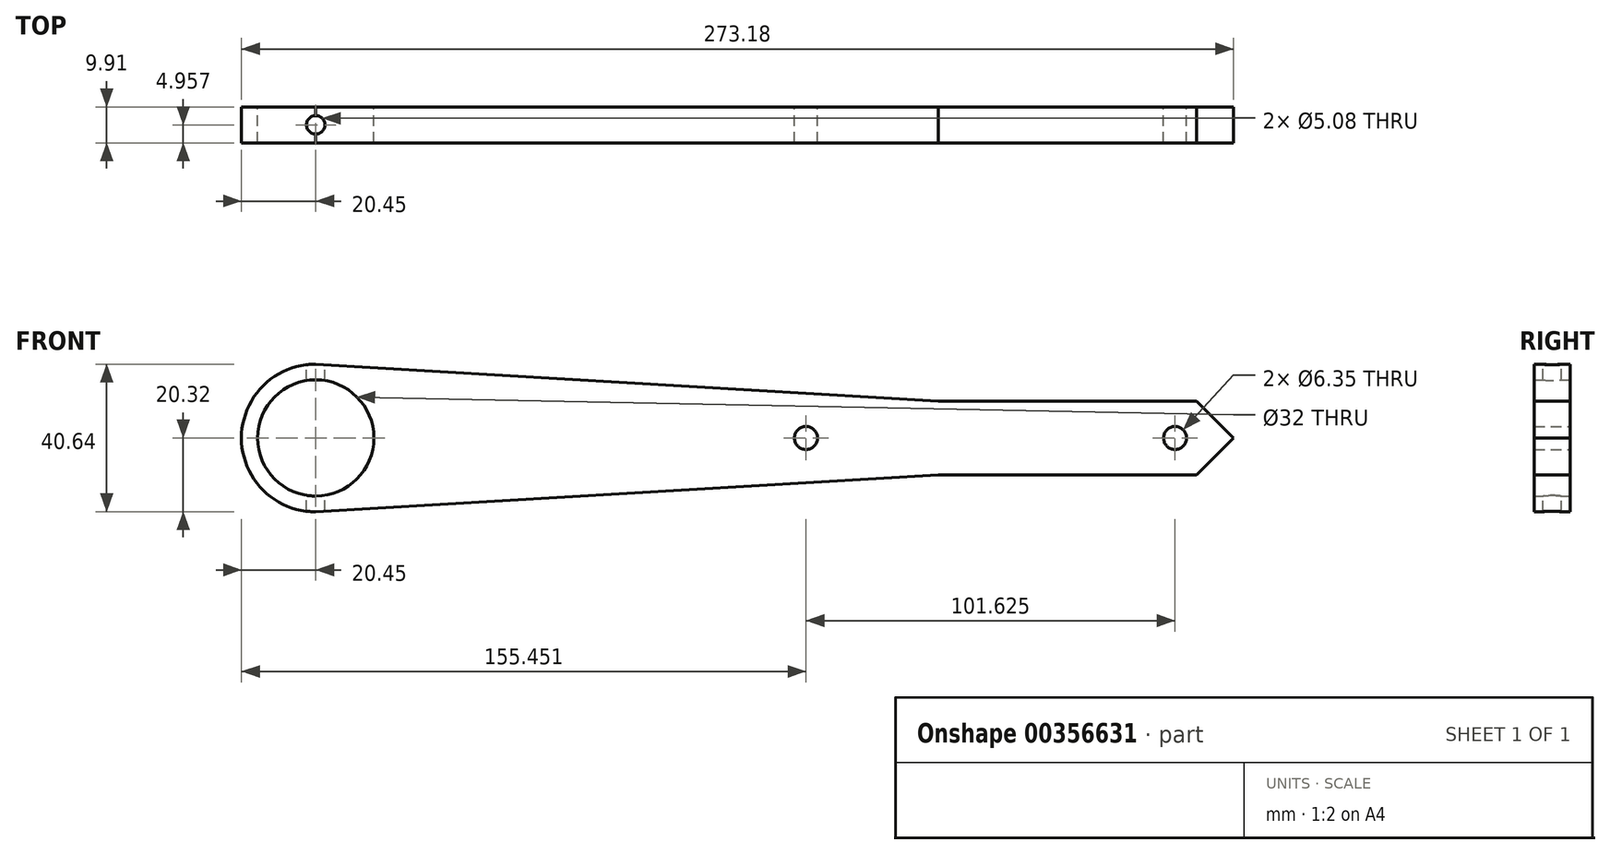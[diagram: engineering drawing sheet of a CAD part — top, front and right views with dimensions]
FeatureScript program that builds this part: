
annotation { "Feature Type Name" : "Feature", "Feature Type Description" : "" }
export const myFeature = defineFeature(function(context is Context, id is Id, definition is map)
    precondition{}
    {
        {
            var Q0;
            Q0=qCreatedBy(makeId("Front.planeOp"),FACE);
            var sketch = newSketch(context, id + "F0", { "sketchPlane" : qUnion([Q0])});
            skLineSegment(sketch, "E0.bottom", {"start": v(40.64, -10.16) * mm, "end": v(-40.64, -10.16) * mm});
            skLineSegment(sketch, "E0.top", {"start": v(40.64, 10.16) * mm, "end": v(-40.64, 10.16) * mm});
            skLineSegment(sketch, "E0.left", {"start": v(40.64, -10.16) * mm, "end": v(40.64, 10.16) * mm});
            skPoint(sketch, "E0.middle", {"position": v(0, 0) * mm});
            skLineSegment(sketch, "E1.bottom", {"start": v(-212.1, -20.32) * mm, "end": v(-212.36, -20.32) * mm});
            skLineSegment(sketch, "E1.top", {"start": v(-212.09, 20.32) * mm, "end": v(-212.36, 20.32) * mm});
            skLineSegment(sketch, "E1.right", {"start": v(-232.4, -2.34) * mm, "end": v(-232.4, 2.34) * mm});
            skPoint(sketch, "E1.middle", {"position": v(-212.1, 0) * mm});
            skCircle(sketch, "E2", {"center": v(-212.1, 0) * mm, "radius": 16 * mm});
            skArc(sketch, "E3", {"start": v(-212.09, 20.32) * mm, "mid": v(-232.54, 0) * mm, "end": v(-212.1, -20.32) * mm});
            skPoint(sketch, "E4.orphan", {"position": v(-232.4, 20.32) * mm});
            skPoint(sketch, "E5.orphan", {"position": v(-232.4, -20.32) * mm});
            skCircle(sketch, "E6", {"center": v(-77.09, 0) * mm, "radius": 3.18 * mm});
            skCircle(sketch, "E7", {"center": v(24.54, 0) * mm, "radius": 3.18 * mm});
            skLineSegment(sketch, "E8", {"start": v(-212.1, -20.32) * mm, "end": v(-40.64, -10.16) * mm});
            skLineSegment(sketch, "E9", {"start": v(-212.09, 20.32) * mm, "end": v(-40.64, 10.16) * mm});
            skLineSegment(sketch, "E10", {"start": v(-212.09, 31.09) * mm, "end": v(-212.09, -33.26) * mm, "construction": true});
            skSolve(sketch);
        }
        {
            var Q0;
            Q0 = qSketchRegion(id + "F0", true);
            extrude(context, id + "F1", {"entities" : qUnion([Q0]), "depth" : 9.9 * mm});
        }
        {
            var Q0;
            Q0=makeQuery(id+"F1.opExtrude","CAP_FACE",FACE,{"disambiguationData":[OSD([sQuery(id+"F0.wireOp",EDGE,"E0.bottom"),sQuery(id+"F0.wireOp",EDGE,"E0.top"),sQuery(id+"F0.wireOp",EDGE,"E0.left"),sQuery(id+"F0.wireOp",EDGE,"E2"),sQuery(id+"F0.wireOp",EDGE,"E3"),sQuery(id+"F0.wireOp",EDGE,"E6"),sQuery(id+"F0.wireOp",EDGE,"E7"),sQuery(id+"F0.wireOp",EDGE,"E8"),sQuery(id+"F0.wireOp",EDGE,"E9")])],"isStart":false});
            var sketch = newSketch(context, id + "F2", { "sketchPlane" : qUnion([Q0])});
            skArc(sketch, "E11.0", {"start": v(-192.22, -12.78) * mm, "mid": v(-188.48, -0.77) * mm, "end": v(-191.44, 11.46) * mm});
            skArc(sketch, "E12.0", {"start": v(-86.52, 5.25) * mm, "mid": v(-87.86, -0.73) * mm, "end": v(-85.73, -6.47) * mm});
            skLineSegment(sketch, "E13.0", {"start": v(-191.44, 11.46) * mm, "end": v(-86.52, 5.25) * mm});
            skLineSegment(sketch, "E14.0", {"start": v(-192.22, -12.78) * mm, "end": v(-85.73, -6.47) * mm});
            skSolve(sketch);
        }
        {
            var Q0;
            Q0=makeQuery(id+"F1.opExtrude","CAP_FACE",FACE,{"disambiguationData":[OSD([sQuery(id+"F0.wireOp",EDGE,"E0.bottom"),sQuery(id+"F0.wireOp",EDGE,"E0.top"),sQuery(id+"F0.wireOp",EDGE,"E0.left"),sQuery(id+"F0.wireOp",EDGE,"E2"),sQuery(id+"F0.wireOp",EDGE,"E3"),sQuery(id+"F0.wireOp",EDGE,"E6"),sQuery(id+"F0.wireOp",EDGE,"E7"),sQuery(id+"F0.wireOp",EDGE,"E8"),sQuery(id+"F0.wireOp",EDGE,"E9")])],"isStart":false});
            var sketch = newSketch(context, id + "F3", { "sketchPlane" : qUnion([Q0])});
            skLineSegment(sketch, "E15", {"start": v(-191.44, 11.46) * mm, "end": v(-138.98, -9.63) * mm});
            skLineSegment(sketch, "E16", {"start": v(-138.98, -9.63) * mm, "end": v(-86.52, 5.25) * mm});
            skLineSegment(sketch, "E17", {"start": v(-85.73, -6.47) * mm, "end": v(-138.98, 8.35) * mm});
            skLineSegment(sketch, "E18", {"start": v(-138.98, 8.35) * mm, "end": v(-192.22, -12.78) * mm});
            skLineSegment(sketch, "E19.0", {"start": v(-190.84, 12.94) * mm, "end": v(-138.39, -8.15) * mm});
            skLineSegment(sketch, "E20.0", {"start": v(-192.03, 9.99) * mm, "end": v(-139.57, -11.1) * mm});
            skLineSegment(sketch, "E21.0", {"start": v(-139.57, 9.83) * mm, "end": v(-192.81, -11.3) * mm});
            skLineSegment(sketch, "E22.0", {"start": v(-138.4, 6.88) * mm, "end": v(-191.64, -14.26) * mm});
            skLineSegment(sketch, "E23.0", {"start": v(-85.3, -4.94) * mm, "end": v(-138.55, 9.88) * mm});
            skLineSegment(sketch, "E24.0", {"start": v(-86.16, -8) * mm, "end": v(-139.4, 6.82) * mm});
            skLineSegment(sketch, "E25.0", {"start": v(-138.54, -11.15) * mm, "end": v(-86.1, 3.72) * mm});
            skLineSegment(sketch, "E26.0", {"start": v(-139.41, -8.1) * mm, "end": v(-86.96, 6.77) * mm});
            skLineSegment(sketch, "E27", {"start": v(-192.03, 9.99) * mm, "end": v(-190.84, 12.94) * mm});
            skSolve(sketch);
        }
        {
            var Q0;
            {var subQ0=sQuery(id+"F3.wireOp",EDGE,"E21.0");var subQ1=sQuery(id+"F3.wireOp",EDGE,"E15");var subQ2=makeQuery(id+"F3.imprint","INTERSECT",VERTEX,{"derivedFrom":[subQ1,subQ0]});Q0=makeQuery(id+"F3.imprint","IMPRINT",FACE,{"disambiguationData":[TD([[makeQuery(id+"F3.imprint","IMPRINT",EDGE,{"disambiguationData":[TD([[subQ2,-1.0]])],"derivedFrom":subQ1}),1.0]])]});}
            var Q1;
            {var subQ0=sQuery(id+"F3.wireOp",EDGE,"E21.0");var subQ1=sQuery(id+"F3.wireOp",EDGE,"E15");var subQ2=makeQuery(id+"F3.imprint","INTERSECT",VERTEX,{"derivedFrom":[subQ1,subQ0]});Q1=makeQuery(id+"F3.imprint","IMPRINT",FACE,{"disambiguationData":[TD([[makeQuery(id+"F3.imprint","IMPRINT",EDGE,{"disambiguationData":[TD([[subQ2,-1.0]])],"derivedFrom":subQ1}),-1.0]])]});}
            var Q2;
            {var subQ0=sQuery(id+"F3.wireOp",EDGE,"E18");var subQ1=sQuery(id+"F3.wireOp",EDGE,"E15");var subQ2=makeQuery(id+"F3.imprint","INTERSECT",VERTEX,{"derivedFrom":[subQ1,subQ0]});Q2=makeQuery(id+"F3.imprint","IMPRINT",FACE,{"disambiguationData":[TD([[makeQuery(id+"F3.imprint","IMPRINT",EDGE,{"disambiguationData":[TD([[subQ2,-1.0]])],"derivedFrom":subQ1}),1.0]])]});}
            var Q3;
            {var subQ0=sQuery(id+"F3.wireOp",EDGE,"E18");var subQ1=sQuery(id+"F3.wireOp",EDGE,"E15");var subQ2=makeQuery(id+"F3.imprint","INTERSECT",VERTEX,{"derivedFrom":[subQ1,subQ0]});Q3=makeQuery(id+"F3.imprint","IMPRINT",FACE,{"disambiguationData":[TD([[makeQuery(id+"F3.imprint","IMPRINT",EDGE,{"disambiguationData":[TD([[subQ2,-1.0]])],"derivedFrom":subQ1}),-1.0]])]});}
            var Q4;
            {var subQ0=sQuery(id+"F3.wireOp",EDGE,"E24.0");var subQ1=sQuery(id+"F3.wireOp",EDGE,"E16");var subQ2=makeQuery(id+"F3.imprint","INTERSECT",VERTEX,{"derivedFrom":[subQ1,subQ0]});Q4=makeQuery(id+"F3.imprint","IMPRINT",FACE,{"disambiguationData":[TD([[makeQuery(id+"F3.imprint","IMPRINT",EDGE,{"disambiguationData":[TD([[subQ2,-1.0]])],"derivedFrom":subQ1}),-1.0]])]});}
            var Q5;
            {var subQ0=sQuery(id+"F3.wireOp",EDGE,"E24.0");var subQ1=sQuery(id+"F3.wireOp",EDGE,"E16");var subQ2=makeQuery(id+"F3.imprint","INTERSECT",VERTEX,{"derivedFrom":[subQ1,subQ0]});Q5=makeQuery(id+"F3.imprint","IMPRINT",FACE,{"disambiguationData":[TD([[makeQuery(id+"F3.imprint","IMPRINT",EDGE,{"disambiguationData":[TD([[subQ2,-1.0]])],"derivedFrom":subQ1}),1.0]])]});}
            var Q6;
            {var subQ0=sQuery(id+"F3.wireOp",EDGE,"E17");var subQ1=sQuery(id+"F3.wireOp",EDGE,"E16");var subQ2=makeQuery(id+"F3.imprint","INTERSECT",VERTEX,{"derivedFrom":[subQ1,subQ0]});Q6=makeQuery(id+"F3.imprint","IMPRINT",FACE,{"disambiguationData":[TD([[makeQuery(id+"F3.imprint","IMPRINT",EDGE,{"disambiguationData":[TD([[subQ2,-1.0]])],"derivedFrom":subQ1}),-1.0]])]});}
            var Q7;
            {var subQ0=sQuery(id+"F3.wireOp",EDGE,"E17");var subQ1=sQuery(id+"F3.wireOp",EDGE,"E16");var subQ2=makeQuery(id+"F3.imprint","INTERSECT",VERTEX,{"derivedFrom":[subQ1,subQ0]});Q7=makeQuery(id+"F3.imprint","IMPRINT",FACE,{"disambiguationData":[TD([[makeQuery(id+"F3.imprint","IMPRINT",EDGE,{"disambiguationData":[TD([[subQ2,-1.0]])],"derivedFrom":subQ1}),1.0]])]});}
            var Q8;
            {var subQ3=sQuery(id+"F3.wireOp",EDGE,"E19.0");var subQ5=sQuery(id+"F3.wireOp",EDGE,"E26.0");var subQ6=makeQuery(id+"F3.imprint","INTERSECT",VERTEX,{"derivedFrom":[subQ3,subQ5]});Q8=makeQuery(id+"F3.imprint","IMPRINT",FACE,{"disambiguationData":[TD([[makeQuery(id+"F3.imprint","IMPRINT",EDGE,{"disambiguationData":[TD([[subQ6,1.0]])],"derivedFrom":subQ3}),-1.0]])]});}
            var Q9;
            {var subQ3=sQuery(id+"F3.wireOp",EDGE,"E19.0");var subQ5=sQuery(id+"F3.wireOp",EDGE,"E18");var subQ6=makeQuery(id+"F3.imprint","INTERSECT",VERTEX,{"derivedFrom":[subQ5,subQ3]});Q9=makeQuery(id+"F3.imprint","IMPRINT",FACE,{"disambiguationData":[TD([[makeQuery(id+"F3.imprint","IMPRINT",EDGE,{"disambiguationData":[TD([[subQ6,-1.0]])],"derivedFrom":subQ3}),1.0]])]});}
            var Q10;
            {var subQ0=sQuery(id+"F3.wireOp",EDGE,"E27");var subQ1=sQuery(id+"F3.wireOp",EDGE,"E19.0");var subQ2=makeQuery(id+"F3.imprint","INTERSECT",VERTEX,{"derivedFrom":[subQ1,subQ0]});Q10=makeQuery(id+"F3.imprint","IMPRINT",FACE,{"disambiguationData":[TD([[makeQuery(id+"F3.imprint","IMPRINT",EDGE,{"disambiguationData":[TD([[subQ2,-1.0]])],"derivedFrom":subQ1}),-1.0]])]});}
            var Q11;
            {var subQ0=sQuery(id+"F3.wireOp",EDGE,"E27");var subQ1=sQuery(id+"F3.wireOp",EDGE,"E20.0");var subQ2=makeQuery(id+"F3.imprint","INTERSECT",VERTEX,{"derivedFrom":[subQ1,subQ0]});Q11=makeQuery(id+"F3.imprint","IMPRINT",FACE,{"disambiguationData":[TD([[makeQuery(id+"F3.imprint","IMPRINT",EDGE,{"disambiguationData":[TD([[subQ2,-1.0]])],"derivedFrom":subQ1}),1.0]])]});}
            var Q12;
            {var subQ3=sQuery(id+"F3.wireOp",EDGE,"E21.0");var subQ5=sQuery(id+"F3.wireOp",EDGE,"E19.0");var subQ6=makeQuery(id+"F3.imprint","INTERSECT",VERTEX,{"derivedFrom":[subQ5,subQ3]});Q12=makeQuery(id+"F3.imprint","IMPRINT",FACE,{"disambiguationData":[TD([[makeQuery(id+"F3.imprint","IMPRINT",EDGE,{"disambiguationData":[TD([[subQ6,1.0]])],"derivedFrom":subQ5}),-1.0]])]});}
            var Q13;
            {var subQ0=sQuery(id+"F3.wireOp",EDGE,"E18");var subQ3=sQuery(id+"F3.wireOp",EDGE,"E20.0");var subQ4=makeQuery(id+"F3.imprint","INTERSECT",VERTEX,{"derivedFrom":[subQ0,subQ3]});Q13=makeQuery(id+"F3.imprint","IMPRINT",FACE,{"disambiguationData":[TD([[makeQuery(id+"F3.imprint","IMPRINT",EDGE,{"disambiguationData":[TD([[subQ4,1.0]])],"derivedFrom":subQ3}),-1.0]])]});}
            var Q14;
            {var subQ0=sQuery(id+"F3.wireOp",EDGE,"E18");var subQ3=sQuery(id+"F3.wireOp",EDGE,"E20.0");var subQ4=makeQuery(id+"F3.imprint","INTERSECT",VERTEX,{"derivedFrom":[subQ0,subQ3]});Q14=makeQuery(id+"F3.imprint","IMPRINT",FACE,{"disambiguationData":[TD([[makeQuery(id+"F3.imprint","IMPRINT",EDGE,{"disambiguationData":[TD([[subQ4,-1.0]])],"derivedFrom":subQ3}),-1.0]])]});}
            var Q15;
            {var subQ3=sQuery(id+"F3.wireOp",EDGE,"E26.0");var subQ5=sQuery(id+"F3.wireOp",EDGE,"E23.0");var subQ6=makeQuery(id+"F3.imprint","INTERSECT",VERTEX,{"derivedFrom":[subQ5,subQ3]});Q15=makeQuery(id+"F3.imprint","IMPRINT",FACE,{"disambiguationData":[TD([[makeQuery(id+"F3.imprint","IMPRINT",EDGE,{"disambiguationData":[TD([[subQ6,-1.0]])],"derivedFrom":subQ5}),1.0]])]});}
            var Q16;
            {var subQ0=sQuery(id+"F3.wireOp",EDGE,"E18");var subQ3=sQuery(id+"F3.wireOp",EDGE,"E19.0");var subQ4=makeQuery(id+"F3.imprint","INTERSECT",VERTEX,{"derivedFrom":[subQ0,subQ3]});Q16=makeQuery(id+"F3.imprint","IMPRINT",FACE,{"disambiguationData":[TD([[makeQuery(id+"F3.imprint","IMPRINT",EDGE,{"disambiguationData":[TD([[subQ4,1.0]])],"derivedFrom":subQ3}),1.0]])]});}
            var Q17;
            {var subQ0=sQuery(id+"F3.wireOp",EDGE,"E16");var subQ3=sQuery(id+"F3.wireOp",EDGE,"E23.0");var subQ4=makeQuery(id+"F3.imprint","INTERSECT",VERTEX,{"derivedFrom":[subQ0,subQ3]});Q17=makeQuery(id+"F3.imprint","IMPRINT",FACE,{"disambiguationData":[TD([[makeQuery(id+"F3.imprint","IMPRINT",EDGE,{"disambiguationData":[TD([[subQ4,1.0]])],"derivedFrom":subQ3}),-1.0]])]});}
            var Q18;
            {var subQ0=sQuery(id+"F3.wireOp",EDGE,"E16");var subQ3=sQuery(id+"F3.wireOp",EDGE,"E23.0");var subQ4=makeQuery(id+"F3.imprint","INTERSECT",VERTEX,{"derivedFrom":[subQ0,subQ3]});Q18=makeQuery(id+"F3.imprint","IMPRINT",FACE,{"disambiguationData":[TD([[makeQuery(id+"F3.imprint","IMPRINT",EDGE,{"disambiguationData":[TD([[subQ4,-1.0]])],"derivedFrom":subQ3}),-1.0]])]});}
            var Q19;
            {var subQ3=sQuery(id+"F3.wireOp",EDGE,"E25.0");var subQ5=sQuery(id+"F3.wireOp",EDGE,"E23.0");var subQ6=makeQuery(id+"F3.imprint","INTERSECT",VERTEX,{"derivedFrom":[subQ5,subQ3]});Q19=makeQuery(id+"F3.imprint","IMPRINT",FACE,{"disambiguationData":[TD([[makeQuery(id+"F3.imprint","IMPRINT",EDGE,{"disambiguationData":[TD([[subQ6,1.0]])],"derivedFrom":subQ5}),1.0]])]});}
            var Q20;
            {var subQ3=sQuery(id+"F3.wireOp",EDGE,"E25.0");var subQ5=sQuery(id+"F3.wireOp",EDGE,"E24.0");var subQ6=makeQuery(id+"F3.imprint","INTERSECT",VERTEX,{"derivedFrom":[subQ5,subQ3]});Q20=makeQuery(id+"F3.imprint","IMPRINT",FACE,{"disambiguationData":[TD([[makeQuery(id+"F3.imprint","IMPRINT",EDGE,{"disambiguationData":[TD([[subQ6,1.0]])],"derivedFrom":subQ5}),-1.0]])]});}
            var Q21;
            {var subQ0=sQuery(id+"F3.wireOp",EDGE,"E16");var subQ3=sQuery(id+"F3.wireOp",EDGE,"E24.0");var subQ4=makeQuery(id+"F3.imprint","INTERSECT",VERTEX,{"derivedFrom":[subQ0,subQ3]});Q21=makeQuery(id+"F3.imprint","IMPRINT",FACE,{"disambiguationData":[TD([[makeQuery(id+"F3.imprint","IMPRINT",EDGE,{"disambiguationData":[TD([[subQ4,1.0]])],"derivedFrom":subQ3}),1.0]])]});}
            var Q22;
            {var subQ3=sQuery(id+"F3.wireOp",EDGE,"E22.0");var subQ5=sQuery(id+"F3.wireOp",EDGE,"E20.0");var subQ6=makeQuery(id+"F3.imprint","INTERSECT",VERTEX,{"derivedFrom":[subQ5,subQ3]});Q22=makeQuery(id+"F3.imprint","IMPRINT",FACE,{"disambiguationData":[TD([[makeQuery(id+"F3.imprint","IMPRINT",EDGE,{"disambiguationData":[TD([[subQ6,-1.0]])],"derivedFrom":subQ5}),1.0]])]});}
            var Q23;
            {var subQ3=sQuery(id+"F3.wireOp",EDGE,"E21.0");var subQ5=sQuery(id+"F3.wireOp",EDGE,"E20.0");var subQ6=makeQuery(id+"F3.imprint","INTERSECT",VERTEX,{"derivedFrom":[subQ5,subQ3]});Q23=makeQuery(id+"F3.imprint","IMPRINT",FACE,{"disambiguationData":[TD([[makeQuery(id+"F3.imprint","IMPRINT",EDGE,{"disambiguationData":[TD([[subQ6,1.0]])],"derivedFrom":subQ5}),1.0]])]});}
            extrude(context, id + "F4", {"entities" : qUnion([Q0, Q1, Q2, Q3, Q4, Q5, Q6, Q7, Q8, Q9, Q10, Q11, Q12, Q13, Q14, Q15, Q16, Q17, Q18, Q19, Q20, Q21, Q22, Q23]), "operationType" : NewBodyOperationType.ADD, "oppositeDirection" : true, "depth" : 9.9 * mm});
        }
        {
            var Q0;
            Q0=makeQuery(id+"F4.boolean.opBoolean","MERGE",FACE,{"derivedFrom":[makeQuery(id+"F1.opExtrude","CAP_FACE",FACE,{"disambiguationData":[OSD([sQuery(id+"F0.wireOp",EDGE,"E0.bottom"),sQuery(id+"F0.wireOp",EDGE,"E0.top"),sQuery(id+"F0.wireOp",EDGE,"E0.left"),sQuery(id+"F0.wireOp",EDGE,"E2"),sQuery(id+"F0.wireOp",EDGE,"E3"),sQuery(id+"F0.wireOp",EDGE,"E6"),sQuery(id+"F0.wireOp",EDGE,"E7"),sQuery(id+"F0.wireOp",EDGE,"E8"),sQuery(id+"F0.wireOp",EDGE,"E9")])],"isStart":false}),makeQuery(id+"F4.opExtrude","CAP_FACE",FACE,{"disambiguationData":[OSD([sQuery(id+"F2.wireOp",EDGE,"E11.0"),sQuery(id+"F2.wireOp",EDGE,"E12.0"),sQuery(id+"F2.wireOp",EDGE,"E13.0"),sQuery(id+"F2.wireOp",EDGE,"E14.0"),sQuery(id+"F3.wireOp",EDGE,"E19.0"),sQuery(id+"F3.wireOp",EDGE,"E20.0"),sQuery(id+"F3.wireOp",EDGE,"E21.0"),sQuery(id+"F3.wireOp",EDGE,"E22.0"),sQuery(id+"F3.wireOp",EDGE,"E23.0"),sQuery(id+"F3.wireOp",EDGE,"E24.0"),sQuery(id+"F3.wireOp",EDGE,"E25.0"),sQuery(id+"F3.wireOp",EDGE,"E26.0"),sQuery(id+"F3.wireOp",EDGE,"E27")])],"isStart":true})]});
            var sketch = newSketch(context, id + "F5", { "sketchPlane" : qUnion([Q0])});
            skLineSegment(sketch, "E28.0.left", {"start": v(-55.02, 4.38) * mm, "end": v(2.47, 4.38) * mm});
            skLineSegment(sketch, "E28.0.right", {"start": v(-55.02, -4.38) * mm, "end": v(2.47, -4.38) * mm});
            skLineSegment(sketch, "E29", {"start": v(-55.02, -4.38) * mm, "end": v(-69.47, 0) * mm});
            skLineSegment(sketch, "E30", {"start": v(-69.47, 0) * mm, "end": v(-55.02, 4.38) * mm});
            skLineSegment(sketch, "E31", {"start": v(2.47, 4.38) * mm, "end": v(16.92, 0) * mm});
            skLineSegment(sketch, "E32", {"start": v(16.92, 0) * mm, "end": v(2.47, -4.38) * mm});
            skLineSegment(sketch, "E33", {"start": v(-26.28, 4.38) * mm, "end": v(-55.02, -4.38) * mm});
            skLineSegment(sketch, "E34", {"start": v(-55.02, 4.38) * mm, "end": v(-26.28, -4.38) * mm});
            skLineSegment(sketch, "E35", {"start": v(-26.28, -4.38) * mm, "end": v(-26.28, 4.38) * mm});
            skLineSegment(sketch, "E36", {"start": v(2.47, -4.38) * mm, "end": v(-26.28, 4.38) * mm});
            skLineSegment(sketch, "E37", {"start": v(-26.28, -4.38) * mm, "end": v(2.47, 4.38) * mm});
            skLineSegment(sketch, "E38.0", {"start": v(-27.3, 5.13) * mm, "end": v(-56.77, -3.85) * mm});
            skLineSegment(sketch, "E39.0", {"start": v(-22.8, 4.38) * mm, "end": v(-57.09, -6.07) * mm});
            skLineSegment(sketch, "E40.0", {"start": v(-56.77, 3.85) * mm, "end": v(-27.3, -5.13) * mm});
            skLineSegment(sketch, "E41.0", {"start": v(4.22, -3.85) * mm, "end": v(-26.64, 5.55) * mm});
            skLineSegment(sketch, "E42.0", {"start": v(3.15, -5.65) * mm, "end": v(-27.24, 3.6) * mm});
            skLineSegment(sketch, "E43.0", {"start": v(-26.64, -5.55) * mm, "end": v(4.22, 3.85) * mm});
            skLineSegment(sketch, "E44.0", {"start": v(-27.24, -3.61) * mm, "end": v(3.15, 5.65) * mm});
            skLineSegment(sketch, "E45.0", {"start": v(-57.09, 6.07) * mm, "end": v(-22.8, -4.38) * mm});
            skLineSegment(sketch, "E46", {"start": v(-56.77, -3.85) * mm, "end": v(-56.77, 3.85) * mm});
            skLineSegment(sketch, "E47", {"start": v(4.22, 3.85) * mm, "end": v(4.22, -3.85) * mm});
            skSolve(sketch);
        }
        {
            var Q0;
            Q0=makeQuery(id+"F1.opExtrude","SWEPT_EDGE",EDGE,{"disambiguationData":[OSD([sQuery(id+"F0.wireOp",EDGE,"E0.bottom"),sQuery(id+"F0.wireOp",EDGE,"E0.left")])]});
            var Q1;
            Q1=makeQuery(id+"F1.opExtrude","SWEPT_EDGE",EDGE,{"disambiguationData":[OSD([sQuery(id+"F0.wireOp",EDGE,"E0.top"),sQuery(id+"F0.wireOp",EDGE,"E0.left")])]});
            chamfer(context, id + "F6", {"entities" : qUnion([Q0, Q1]), "width" : 10.16 * mm, "tangentPropagation" : true});
        }
        {
            var Q0;
            Q0=qCreatedBy(makeId("Top.planeOp"),FACE);
            var sketch = newSketch(context, id + "F7", { "sketchPlane" : qUnion([Q0])});
            skCircle(sketch, "E48", {"center": v(-212.1, -4.95) * mm, "radius": 2.54 * mm});
            skSolve(sketch);
        }
        {
            var Q0;
            Q0 = qSketchRegion(id + "F7", true);
            extrude(context, id + "F8", {"entities" : qUnion([Q0]), "operationType" : NewBodyOperationType.REMOVE, "oppositeDirection" : true, "depth" : 127 * mm, "symmetric" : true});
        }
    });
